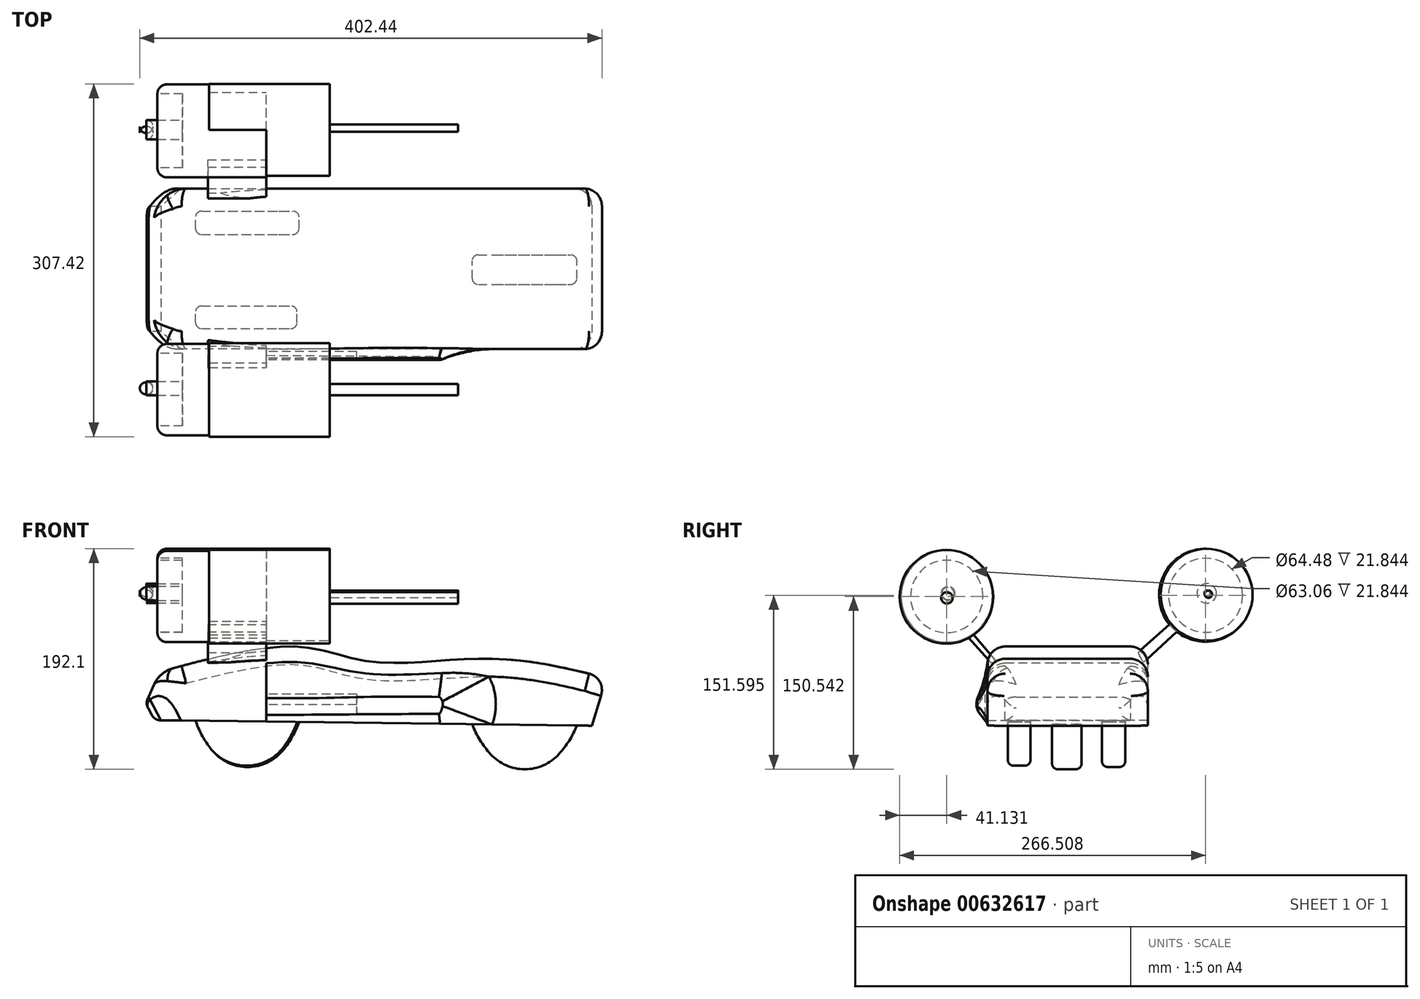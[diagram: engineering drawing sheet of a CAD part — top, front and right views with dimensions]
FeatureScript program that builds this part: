
annotation { "Feature Type Name" : "Feature", "Feature Type Description" : "" }
export const myFeature = defineFeature(function(context is Context, id is Id, definition is map)
    precondition{}
    {
        {
            var Q0;
            Q0=qCreatedBy(makeId("Front.planeOp"),FACE);
            var sketch = newSketch(context, id + "F0", { "sketchPlane" : qUnion([Q0])});
            skFitSpline(sketch, "E0", {"points": [v(-111.39, 0) * mm, v(28.2, 27.12) * mm, v(91.16, 14) * mm, v(196.58, 16.62) * mm, v(296.07, 0) * mm], "startDerivative": vector(527.44, 148.04) * mm, "endDerivative": vector(384.86, -95.59) * mm});
            skLineSegment(sketch, "E1", {"start": v(296.07, 0) * mm, "end": v(283.35, -41.68) * mm});
            skLineSegment(sketch, "E2", {"start": v(283.35, -41.68) * mm, "end": v(-91.68, -36.95) * mm});
            skLineSegment(sketch, "E3", {"start": v(-91.68, -36.95) * mm, "end": v(-111.39, 0) * mm});
            skSolve(sketch);
        }
        {
            var Q0;
            Q0 = qSketchRegion(id + "F0", true);
            extrude(context, id + "F1", {"entities" : qUnion([Q0]), "endBound" : BoundingType.SYMMETRIC, "oppositeDirection" : true, "depth" : 139.65 * mm, "offsetDistance" : 25.4 * mm});
        }
        {
            var Q0;
            Q0=makeQuery(id+"F1.opExtrude","CAP_EDGE",EDGE,{"disambiguationData":[OSD([sQuery(id+"F0.wireOp",EDGE,"E0")])],"isStart":false});
            var Q1;
            Q1=makeQuery(id+"F1.opExtrude","CAP_EDGE",EDGE,{"disambiguationData":[OSD([sQuery(id+"F0.wireOp",EDGE,"E0")])],"isStart":true});
            fillet(context, id + "F2", {"entities" : qUnion([Q0, Q1]), "radius" : 15.58 * mm, "tangentPropagation" : true, "allowEdgeOverflow" : false});
        }
        {
            var Q0;
            Q0=makeQuery(id+"F1.opExtrude","SWEPT_EDGE",EDGE,{"disambiguationData":[OSD([sQuery(id+"F0.wireOp",EDGE,"E0"),sQuery(id+"F0.wireOp",EDGE,"E1")])]});
            fillet(context, id + "F3", {"entities" : qUnion([Q0]), "radius" : 14.6 * mm, "tangentPropagation" : true, "allowEdgeOverflow" : false});
        }
        {
            var Q0;
            Q0=qCreatedBy(makeId("Right.planeOp"),FACE);
            var sketch = newSketch(context, id + "F4", { "sketchPlane" : qUnion([Q0])});
            skArc(sketch, "E4", {"start": v(-65.26, -9.54) * mm, "mid": v(-79.36, -22.04) * mm, "end": v(-66.86, -36.14) * mm});
            skLineSegment(sketch, "E5", {"start": v(-65.26, -9.54) * mm, "end": v(-66.06, -22.84) * mm});
            skLineSegment(sketch, "E6", {"start": v(-66.86, -36.14) * mm, "end": v(-66.06, -22.84) * mm});
            skSolve(sketch);
        }
        {
            var Q0;
            Q0 = qSketchRegion(id + "F4", true);
            extrude(context, id + "F5", {"entities" : qUnion([Q0]), "operationType" : NewBodyOperationType.ADD, "depth" : 159.32 * mm, "offsetDistance" : 25.4 * mm});
        }
        {
            var Q0;
            Q0=makeQuery(id+"F5.opExtrude","CAP_EDGE",EDGE,{"disambiguationData":[OSD([sQuery(id+"F4.wireOp",EDGE,"E4")])],"isStart":false});
            var Q1;
            Q1=makeQuery(id+"F3lUEw8ZCyhcsNu_1.1.F5.opExtrude","CAP_EDGE",EDGE,{"disambiguationData":[OSD([sQuery(id+"F4.wireOp",EDGE,"E4")])],"isStart":false});
            fillet(context, id + "F6", {"entities" : qUnion([Q0, Q1]), "radius" : 8.98 * mm, "tangentPropagation" : true, "allowEdgeOverflow" : false});
        }
        {
            var Q0;
            Q0=qCreatedBy(makeId("Right.planeOp"),FACE);
            var sketch = newSketch(context, id + "F7", { "sketchPlane" : qUnion([Q0])});
            skLineSegment(sketch, "E7", {"start": v(72.11, -14.5) * mm, "end": v(72.11, -32.7) * mm});
            skLineSegment(sketch, "E8", {"start": v(72.11, -32.7) * mm, "end": v(72.11, -23.6) * mm});
            skLineSegment(sketch, "E9", {"start": v(72.11, -23.6) * mm, "end": v(72.11, -32.7) * mm});
            skLineSegment(sketch, "E10", {"start": v(77.87, -23.6) * mm, "end": v(72.11, -32.7) * mm});
            skLineSegment(sketch, "E11", {"start": v(77.87, -23.6) * mm, "end": v(72.11, -14.5) * mm});
            skLineSegment(sketch, "E12", {"start": v(-72.12, -14.15) * mm, "end": v(-72.12, -32.4) * mm});
            skLineSegment(sketch, "E13", {"start": v(-72.12, -32.4) * mm, "end": v(-77.78, -23.27) * mm});
            skPoint(sketch, "E13.endSnap0", {"position": v(-72.12, -23.27) * mm});
            skLineSegment(sketch, "E14", {"start": v(-77.78, -23.27) * mm, "end": v(-72.12, -14.15) * mm});
            skSolve(sketch);
        }
        {
            var Q0;
            Q0 = qSketchRegion(id + "F7", true);
            extrude(context, id + "F8", {"entities" : qUnion([Q0]), "operationType" : NewBodyOperationType.REMOVE, "depth" : 78.65 * mm, "offsetDistance" : 25.4 * mm});
        }
        {
            var Q0;
            Q0=makeQuery(id+"F1.opExtrude","CAP_EDGE",EDGE,{"disambiguationData":[OSD([sQuery(id+"F0.wireOp",EDGE,"E3")])],"isStart":false});
            chamfer(context, id + "F9", {"entities" : qUnion([Q0]), "width" : 15.24 * mm, "tangentPropagation" : true});
        }
        {
            var Q0;
            {var subQ0=sQuery(id+"F0.wireOp",EDGE,"E0");Q0=makeQuery(id+"F9.opChamfer","BLEND_EDGE",EDGE,{"blendedFrom":[makeQuery(id+"F1.opExtrude","SWEPT_EDGE",EDGE,{"disambiguationData":[OSD([subQ0,sQuery(id+"F0.wireOp",EDGE,"E3")])]}),makeQuery(id+"F1.opExtrude","SWEPT_FACE",FACE,{"disambiguationData":[OSD([subQ0])]})],"blendedInto":[makeQuery(id+"F1.opExtrude","SWEPT_FACE",FACE,{"disambiguationData":[OSD([subQ0])]})]});}
            fillet(context, id + "F10", {"entities" : qUnion([Q0]), "radius" : 25.21 * mm, "tangentPropagation" : true, "allowEdgeOverflow" : false});
        }
        {
            var Q0;
            Q0=qCreatedBy(makeId("Front.planeOp"),FACE);
            var sketch = newSketch(context, id + "F11", { "sketchPlane" : qUnion([Q0])});
            skLineSegment(sketch, "E15", {"start": v(19.53, 27.35) * mm, "end": v(103, 49.29) * mm});
            skLineSegment(sketch, "E16", {"start": v(103, 49.29) * mm, "end": v(187, 37.43) * mm});
            skLineSegment(sketch, "E17", {"start": v(187, 37.43) * mm, "end": v(228.55, 13.52) * mm});
            skLineSegment(sketch, "E18", {"start": v(228.55, 13.52) * mm, "end": v(82.33, 13.52) * mm});
            skLineSegment(sketch, "E19", {"start": v(82.33, 13.52) * mm, "end": v(19.53, 27.35) * mm});
            skSolve(sketch);
        }
        {
            var Q0;
            Q0=makeQuery(id+"F5.boolean.opBoolean","INTERSECT",EDGE,{"disambiguationData":[OD(1.0)],"derivedFrom":[makeQuery(id+"F1.opExtrude","CAP_FACE",FACE,{"disambiguationData":[OSD([sQuery(id+"F0.wireOp",EDGE,"E0"),sQuery(id+"F0.wireOp",EDGE,"E1"),sQuery(id+"F0.wireOp",EDGE,"E2"),sQuery(id+"F0.wireOp",EDGE,"E3")])],"isStart":true}),makeQuery(id+"F5.opExtrude","SWEPT_FACE",FACE,{"disambiguationData":[OSD([sQuery(id+"F4.wireOp",EDGE,"E4")])]})]});
            var Q1;
            Q1=makeQuery(id+"F3lUEw8ZCyhcsNu_1.1.F5.boolean.opBoolean","INTERSECT",EDGE,{"disambiguationData":[OD(1.0)],"derivedFrom":[makeQuery(id+"F1.opExtrude","CAP_FACE",FACE,{"disambiguationData":[OSD([sQuery(id+"F0.wireOp",EDGE,"E0"),sQuery(id+"F0.wireOp",EDGE,"E1"),sQuery(id+"F0.wireOp",EDGE,"E2"),sQuery(id+"F0.wireOp",EDGE,"E3")])],"isStart":false}),makeQuery(id+"F3lUEw8ZCyhcsNu_1.1.F5.opExtrude","SWEPT_FACE",FACE,{"disambiguationData":[OSD([sQuery(id+"F4.wireOp",EDGE,"E4")])]})]});
            fillet(context, id + "F12", {"entities" : qUnion([Q0, Q1]), "radius" : 123.76 * mm, "tangentPropagation" : true, "allowEdgeOverflow" : false});
        }
        {
            var Q0;
            Q0=qCreatedBy(makeId("Top.planeOp"),FACE);
            var sketch = newSketch(context, id + "F13", { "sketchPlane" : qUnion([Q0])});
            skLineSegment(sketch, "E20.bottom", {"start": v(-61.68, -52) * mm, "end": v(26.68, -52) * mm});
            skLineSegment(sketch, "E20.top", {"start": v(-61.68, -32.34) * mm, "end": v(26.68, -32.34) * mm});
            skLineSegment(sketch, "E20.left", {"start": v(-61.68, -52) * mm, "end": v(-61.68, -32.34) * mm});
            skLineSegment(sketch, "E20.right", {"start": v(26.68, -52) * mm, "end": v(26.68, -32.34) * mm});
            skLineSegment(sketch, "E21.bottom", {"start": v(-61.68, 29.92) * mm, "end": v(28.42, 29.92) * mm});
            skLineSegment(sketch, "E21.top", {"start": v(-61.68, 50.23) * mm, "end": v(28.42, 50.23) * mm});
            skLineSegment(sketch, "E21.left", {"start": v(-61.68, 29.92) * mm, "end": v(-61.68, 50.23) * mm});
            skLineSegment(sketch, "E21.right", {"start": v(28.42, 29.92) * mm, "end": v(28.42, 50.23) * mm});
            skLineSegment(sketch, "E22.bottom", {"start": v(179.16, -13.58) * mm, "end": v(270.37, -13.58) * mm});
            skLineSegment(sketch, "E22.top", {"start": v(179.16, 12.15) * mm, "end": v(270.37, 12.15) * mm});
            skLineSegment(sketch, "E22.left", {"start": v(179.16, -13.58) * mm, "end": v(179.16, 12.15) * mm});
            skLineSegment(sketch, "E22.right", {"start": v(270.37, -13.58) * mm, "end": v(270.37, 12.15) * mm});
            skSolve(sketch);
        }
        {
            var Q0;
            Q0 = qSketchRegion(id + "F13", true);
            extrude(context, id + "F14", {"entities" : qUnion([Q0]), "operationType" : NewBodyOperationType.ADD, "oppositeDirection" : true, "depth" : 93.8 * mm, "offsetDistance" : 25.4 * mm});
        }
        {
            var Q0;
            Q0=makeQuery(id+"F14.opExtrude","CAP_EDGE",EDGE,{"disambiguationData":[OSD([sQuery(id+"F13.wireOp",EDGE,"E21.left")])],"isStart":false});
            var Q1;
            Q1=makeQuery(id+"F14.opExtrude","CAP_EDGE",EDGE,{"disambiguationData":[OSD([sQuery(id+"F13.wireOp",EDGE,"E20.left")])],"isStart":false});
            var Q2;
            Q2=makeQuery(id+"F14.opExtrude","CAP_EDGE",EDGE,{"disambiguationData":[OSD([sQuery(id+"F13.wireOp",EDGE,"E21.right")])],"isStart":false});
            var Q3;
            Q3=makeQuery(id+"F14.opExtrude","CAP_EDGE",EDGE,{"disambiguationData":[OSD([sQuery(id+"F13.wireOp",EDGE,"E20.right")])],"isStart":false});
            var Q4;
            Q4=makeQuery(id+"F14.opExtrude","CAP_EDGE",EDGE,{"disambiguationData":[OSD([sQuery(id+"F13.wireOp",EDGE,"E22.left")])],"isStart":false});
            var Q5;
            Q5=makeQuery(id+"F14.opExtrude","CAP_EDGE",EDGE,{"disambiguationData":[OSD([sQuery(id+"F13.wireOp",EDGE,"E22.right")])],"isStart":false});
            fillet(context, id + "F15", {"entities" : qUnion([Q0, Q1, Q2, Q3, Q4, Q5]), "radius" : 83.48 * mm, "tangentPropagation" : true, "allowEdgeOverflow" : false});
        }
        {
            var Q0;
            Q0=makeQuery(id+"F15.opFillet","BLEND_EDGE",EDGE,{"blendedFrom":[makeQuery(id+"F14.opExtrude","CAP_EDGE",EDGE,{"disambiguationData":[OSD([sQuery(id+"F13.wireOp",EDGE,"E22.left")])],"isStart":false}),makeQuery(id+"F14.opExtrude","CAP_EDGE",EDGE,{"disambiguationData":[OSD([sQuery(id+"F13.wireOp",EDGE,"E22.right")])],"isStart":false})],"blendedInto":[]});
            var Q1;
            Q1=makeQuery(id+"F15.opFillet","BLEND_EDGE",EDGE,{"blendedFrom":[makeQuery(id+"F14.opExtrude","CAP_EDGE",EDGE,{"disambiguationData":[OSD([sQuery(id+"F13.wireOp",EDGE,"E21.left")])],"isStart":false}),makeQuery(id+"F14.opExtrude","CAP_EDGE",EDGE,{"disambiguationData":[OSD([sQuery(id+"F13.wireOp",EDGE,"E21.right")])],"isStart":false})],"blendedInto":[]});
            var Q2;
            Q2=makeQuery(id+"F15.opFillet","BLEND_EDGE",EDGE,{"blendedFrom":[makeQuery(id+"F14.opExtrude","CAP_EDGE",EDGE,{"disambiguationData":[OSD([sQuery(id+"F13.wireOp",EDGE,"E20.left")])],"isStart":false}),makeQuery(id+"F14.opExtrude","CAP_EDGE",EDGE,{"disambiguationData":[OSD([sQuery(id+"F13.wireOp",EDGE,"E20.right")])],"isStart":false})],"blendedInto":[]});
            fillet(context, id + "F16", {"entities" : qUnion([Q0, Q1, Q2]), "radius" : 40.13 * mm, "tangentPropagation" : true, "allowEdgeOverflow" : false});
        }
        {
            var Q0;
            Q0=makeQuery(id+"F15.opFillet","BLEND_EDGE",EDGE,{"blendedFrom":[makeQuery(id+"F14.opExtrude","CAP_EDGE",EDGE,{"disambiguationData":[OSD([sQuery(id+"F13.wireOp",EDGE,"E21.right")])],"isStart":false}),makeQuery(id+"F14.opExtrude","SWEPT_FACE",FACE,{"disambiguationData":[OSD([sQuery(id+"F13.wireOp",EDGE,"E21.top")])]})],"blendedInto":[makeQuery(id+"F14.opExtrude","SWEPT_FACE",FACE,{"disambiguationData":[OSD([sQuery(id+"F13.wireOp",EDGE,"E21.top")])]})]});
            var Q1;
            Q1=makeQuery(id+"F15.opFillet","BLEND_EDGE",EDGE,{"blendedFrom":[makeQuery(id+"F14.opExtrude","CAP_EDGE",EDGE,{"disambiguationData":[OSD([sQuery(id+"F13.wireOp",EDGE,"E20.right")])],"isStart":false}),makeQuery(id+"F14.opExtrude","SWEPT_FACE",FACE,{"disambiguationData":[OSD([sQuery(id+"F13.wireOp",EDGE,"E20.top")])]})],"blendedInto":[makeQuery(id+"F14.opExtrude","SWEPT_FACE",FACE,{"disambiguationData":[OSD([sQuery(id+"F13.wireOp",EDGE,"E20.top")])]})]});
            var Q2;
            Q2=makeQuery(id+"F15.opFillet","BLEND_EDGE",EDGE,{"blendedFrom":[makeQuery(id+"F14.opExtrude","CAP_EDGE",EDGE,{"disambiguationData":[OSD([sQuery(id+"F13.wireOp",EDGE,"E22.right")])],"isStart":false}),makeQuery(id+"F14.opExtrude","SWEPT_FACE",FACE,{"disambiguationData":[OSD([sQuery(id+"F13.wireOp",EDGE,"E22.top")])]})],"blendedInto":[makeQuery(id+"F14.opExtrude","SWEPT_FACE",FACE,{"disambiguationData":[OSD([sQuery(id+"F13.wireOp",EDGE,"E22.top")])]})]});
            var Q3;
            Q3=makeQuery(id+"F15.opFillet","BLEND_EDGE",EDGE,{"blendedFrom":[makeQuery(id+"F14.opExtrude","CAP_EDGE",EDGE,{"disambiguationData":[OSD([sQuery(id+"F13.wireOp",EDGE,"E22.right")])],"isStart":false}),makeQuery(id+"F14.opExtrude","SWEPT_FACE",FACE,{"disambiguationData":[OSD([sQuery(id+"F13.wireOp",EDGE,"E22.bottom")])]})],"blendedInto":[makeQuery(id+"F14.opExtrude","SWEPT_FACE",FACE,{"disambiguationData":[OSD([sQuery(id+"F13.wireOp",EDGE,"E22.bottom")])]})]});
            var Q4;
            Q4=makeQuery(id+"F15.opFillet","BLEND_EDGE",EDGE,{"blendedFrom":[makeQuery(id+"F14.opExtrude","CAP_EDGE",EDGE,{"disambiguationData":[OSD([sQuery(id+"F13.wireOp",EDGE,"E20.right")])],"isStart":false}),makeQuery(id+"F14.opExtrude","SWEPT_FACE",FACE,{"disambiguationData":[OSD([sQuery(id+"F13.wireOp",EDGE,"E20.bottom")])]})],"blendedInto":[makeQuery(id+"F14.opExtrude","SWEPT_FACE",FACE,{"disambiguationData":[OSD([sQuery(id+"F13.wireOp",EDGE,"E20.bottom")])]})]});
            var Q5;
            Q5=makeQuery(id+"F15.opFillet","BLEND_EDGE",EDGE,{"blendedFrom":[makeQuery(id+"F14.opExtrude","CAP_EDGE",EDGE,{"disambiguationData":[OSD([sQuery(id+"F13.wireOp",EDGE,"E21.right")])],"isStart":false}),makeQuery(id+"F14.opExtrude","SWEPT_FACE",FACE,{"disambiguationData":[OSD([sQuery(id+"F13.wireOp",EDGE,"E21.bottom")])]})],"blendedInto":[makeQuery(id+"F14.opExtrude","SWEPT_FACE",FACE,{"disambiguationData":[OSD([sQuery(id+"F13.wireOp",EDGE,"E21.bottom")])]})]});
            fillet(context, id + "F17", {"entities" : qUnion([Q0, Q1, Q2, Q3, Q4, Q5]), "radius" : 5.08 * mm, "tangentPropagation" : true, "allowEdgeOverflow" : false});
        }
        {
            var Q0;
            Q0=sQuery(id+"F11.wireOp",EDGE,"E15");
            var Q1;
            Q1=sQuery(id+"F11.wireOp",EDGE,"E19");
            var Q2;
            Q2=sQuery(id+"F11.wireOp",EDGE,"E18");
            var Q3;
            Q3=sQuery(id+"F11.wireOp",EDGE,"E17");
            var Q4;
            Q4=sQuery(id+"F11.wireOp",EDGE,"E16");
            extrude(context, id + "F18", {"bodyType" : ToolBodyType.SURFACE, "surfaceEntities" : qUnion([Q0, Q1, Q2, Q3, Q4]), "endBound" : BoundingType.SYMMETRIC, "depth" : 100.02 * mm, "offsetDistance" : 25.4 * mm});
        }
        {
            var Q0;
            Q0=qCreatedBy(makeId("Right.planeOp"),FACE);
            var sketch = newSketch(context, id + "F19", { "sketchPlane" : qUnion([Q0])});
            skLineSegment(sketch, "E23", {"start": v(65.95, 13.38) * mm, "end": v(109.33, 53.33) * mm});
            skLineSegment(sketch, "E24", {"start": v(109.33, 53.33) * mm, "end": v(103.43, 59.64) * mm});
            skLineSegment(sketch, "E25", {"start": v(103.43, 59.64) * mm, "end": v(61.2, 21.9) * mm});
            skLineSegment(sketch, "E26", {"start": v(61.2, 21.9) * mm, "end": v(65.95, 13.38) * mm});
            skLineSegment(sketch, "E27", {"start": v(-60.68, 12.45) * mm, "end": v(-67.27, 13.56) * mm});
            skLineSegment(sketch, "E28", {"start": v(-67.27, 13.56) * mm, "end": v(-103.78, 54.83) * mm});
            skLineSegment(sketch, "E29", {"start": v(-103.78, 54.83) * mm, "end": v(-105.55, 65.9) * mm});
            skLineSegment(sketch, "E30", {"start": v(-105.55, 65.9) * mm, "end": v(-60.68, 12.45) * mm});
            skCircle(sketch, "E31", {"center": v(121.04, 72.42) * mm, "radius": 40.04 * mm});
            skCircle(sketch, "E32", {"center": v(-105.55, 70.64) * mm, "radius": 40.8 * mm});
            skSolve(sketch);
        }
        {
            var Q0;
            {var subQ0=sQuery(id+"F19.wireOp",EDGE,"E24");Q0=makeQuery(id+"F19.imprint","IMPRINT",FACE,{"disambiguationData":[TD([[makeQuery(id+"F19.imprint","IMPRINT",EDGE,{"derivedFrom":subQ0}),1.0]])]});}
            var Q1;
            {var subQ0=sQuery(id+"F19.wireOp",EDGE,"E26");Q1=makeQuery(id+"F19.imprint","IMPRINT",FACE,{"disambiguationData":[TD([[makeQuery(id+"F19.imprint","IMPRINT",EDGE,{"derivedFrom":subQ0}),1.0]])]});}
            var Q2;
            {var subQ0=sQuery(id+"F19.wireOp",EDGE,"E27");Q2=makeQuery(id+"F19.imprint","IMPRINT",FACE,{"disambiguationData":[TD([[makeQuery(id+"F19.imprint","IMPRINT",EDGE,{"derivedFrom":subQ0}),-1.0]])]});}
            var Q3;
            {var subQ0=sQuery(id+"F19.wireOp",EDGE,"E29");Q3=makeQuery(id+"F19.imprint","IMPRINT",FACE,{"disambiguationData":[TD([[makeQuery(id+"F19.imprint","IMPRINT",EDGE,{"derivedFrom":subQ0}),-1.0]])]});}
            extrude(context, id + "F20", {"entities" : qUnion([Q0, Q1, Q2, Q3]), "operationType" : NewBodyOperationType.ADD, "oppositeDirection" : true, "depth" : 50.96 * mm, "offsetDistance" : 25.4 * mm});
        }
        {
            var Q0;
            {var subQ0=sQuery(id+"F19.wireOp",EDGE,"E24");Q0=makeQuery(id+"F19.imprint","IMPRINT",FACE,{"disambiguationData":[TD([[makeQuery(id+"F19.imprint","IMPRINT",EDGE,{"derivedFrom":subQ0}),-1.0]])]});}
            var Q1;
            {var subQ0=sQuery(id+"F19.wireOp",EDGE,"E29");Q1=makeQuery(id+"F19.imprint","IMPRINT",FACE,{"disambiguationData":[TD([[makeQuery(id+"F19.imprint","IMPRINT",EDGE,{"derivedFrom":subQ0}),1.0]])]});}
            extrude(context, id + "F21", {"entities" : qUnion([Q0, Q1]), "operationType" : NewBodyOperationType.ADD, "oppositeDirection" : true, "depth" : 49.86 * mm, "offsetDistance" : 25.4 * mm});
        }
        {
            var Q0;
            {var subQ0=sQuery(id+"F19.wireOp",EDGE,"E24");Q0=makeQuery(id+"F19.imprint","IMPRINT",FACE,{"disambiguationData":[TD([[makeQuery(id+"F19.imprint","IMPRINT",EDGE,{"derivedFrom":subQ0}),-1.0]])]});}
            var Q1;
            {var subQ0=sQuery(id+"F19.wireOp",EDGE,"E29");Q1=makeQuery(id+"F19.imprint","IMPRINT",FACE,{"disambiguationData":[TD([[makeQuery(id+"F19.imprint","IMPRINT",EDGE,{"derivedFrom":subQ0}),1.0]])]});}
            var Q2;
            {var subQ0=sQuery(id+"F19.wireOp",EDGE,"E29");Q2=makeQuery(id+"F19.imprint","IMPRINT",FACE,{"disambiguationData":[TD([[makeQuery(id+"F19.imprint","IMPRINT",EDGE,{"derivedFrom":subQ0}),-1.0]])]});}
            var Q3;
            {var subQ0=sQuery(id+"F19.wireOp",EDGE,"E24");Q3=makeQuery(id+"F19.imprint","IMPRINT",FACE,{"disambiguationData":[TD([[makeQuery(id+"F19.imprint","IMPRINT",EDGE,{"derivedFrom":subQ0}),1.0]])]});}
            extrude(context, id + "F22", {"entities" : qUnion([Q0, Q1, Q2, Q3]), "operationType" : NewBodyOperationType.ADD, "depth" : 55.22 * mm, "offsetDistance" : 25.4 * mm});
        }
        {
            var Q0;
            Q0=qCreatedBy(makeId("Right.planeOp"),FACE);
            var sketch = newSketch(context, id + "F23", { "sketchPlane" : qUnion([Q0])});
            skCircle(sketch, "E33", {"center": v(-105.02, 70.59) * mm, "radius": 28.06 * mm});
            skCircle(sketch, "E34", {"center": v(-105.02, 70.59) * mm, "radius": 13.97 * mm});
            skCircle(sketch, "E35", {"center": v(121.55, 72.17) * mm, "radius": 26.48 * mm});
            skCircle(sketch, "E36", {"center": v(121.55, 72.17) * mm, "radius": 13.98 * mm});
            skSolve(sketch);
        }
        {
            var Q0;
            Q0=sQuery(id+"F23.wireOp",EDGE,"E33");
            var Q1;
            Q1=sQuery(id+"F23.wireOp",EDGE,"E35");
            extrude(context, id + "F24", {"bodyType" : ToolBodyType.SURFACE, "surfaceEntities" : qUnion([Q0, Q1]), "depth" : 97.47 * mm, "offsetDistance" : 25.4 * mm});
        }
        {
            var Q0;
            Q0=sQuery(id+"F23.wireOp",EDGE,"E36");
            var Q1;
            Q1=sQuery(id+"F23.wireOp",EDGE,"E34");
            extrude(context, id + "F25", {"bodyType" : ToolBodyType.SURFACE, "surfaceEntities" : qUnion([Q0, Q1]), "depth" : 146.7 * mm, "offsetDistance" : 25.4 * mm});
        }
        {
            var Q0;
            Q0=qCreatedBy(makeId("Right.planeOp"),FACE);
            var sketch = newSketch(context, id + "F26", { "sketchPlane" : qUnion([Q0])});
            skCircle(sketch, "E37", {"center": v(120.17, 71.97) * mm, "radius": 40.5 * mm});
            skCircle(sketch, "E38", {"center": v(-105.2, 70.91) * mm, "radius": 39.8 * mm});
            skSolve(sketch);
        }
        {
            var Q0;
            Q0 = qSketchRegion(id + "F26", true);
            extrude(context, id + "F27", {"entities" : qUnion([Q0]), "operationType" : NewBodyOperationType.ADD, "oppositeDirection" : true, "depth" : 94.92 * mm, "offsetDistance" : 25.4 * mm});
        }
        {
            var Q0;
            Q0=makeQuery(id+"F27.opExtrude","CAP_EDGE",EDGE,{"disambiguationData":[OSD([sQuery(id+"F26.wireOp",EDGE,"E37")])],"isStart":false});
            var Q1;
            Q1=makeQuery(id+"F27.opExtrude","CAP_EDGE",EDGE,{"disambiguationData":[OSD([sQuery(id+"F26.wireOp",EDGE,"E38")])],"isStart":false});
            fillet(context, id + "F28", {"entities" : qUnion([Q0, Q1]), "radius" : 8.26 * mm, "tangentPropagation" : true, "allowEdgeOverflow" : false});
        }
        {
            var Q0;
            Q0=makeQuery(id+"F27.opExtrude","CAP_FACE",FACE,{"disambiguationData":[OSD([sQuery(id+"F26.wireOp",EDGE,"E37")])],"isStart":false});
            var Q1;
            Q1=makeQuery(id+"F27.opExtrude","CAP_FACE",FACE,{"disambiguationData":[OSD([sQuery(id+"F26.wireOp",EDGE,"E38")])],"isStart":false});
            extrude(context, id + "F29", {"entities" : qUnion([Q0, Q1]), "operationType" : NewBodyOperationType.REMOVE, "oppositeDirection" : true, "depth" : 21.84 * mm, "offsetDistance" : 25.4 * mm});
        }
        {
            var Q0;
            Q0=qCreatedBy(makeId("Right.planeOp"),FACE);
            var sketch = newSketch(context, id + "F30", { "sketchPlane" : qUnion([Q0])});
            skCircle(sketch, "E39", {"center": v(121.18, 73.6) * mm, "radius": 8.49 * mm});
            skCircle(sketch, "E40", {"center": v(-104.1, 73.62) * mm, "radius": 6.08 * mm});
            skSolve(sketch);
        }
        {
            var Q0;
            Q0 = qSketchRegion(id + "F30", true);
            extrude(context, id + "F31", {"entities" : qUnion([Q0]), "operationType" : NewBodyOperationType.ADD, "oppositeDirection" : true, "depth" : 110.23 * mm, "offsetDistance" : 25.4 * mm});
        }
        {
            var Q0;
            Q0=makeQuery(id+"F31.opExtrude","CAP_EDGE",EDGE,{"disambiguationData":[OSD([sQuery(id+"F30.wireOp",EDGE,"E40")])],"isStart":false});
            var Q1;
            Q1=makeQuery(id+"F31.opExtrude","CAP_EDGE",EDGE,{"disambiguationData":[OSD([sQuery(id+"F30.wireOp",EDGE,"E39")])],"isStart":false});
            fillet(context, id + "F32", {"entities" : qUnion([Q0, Q1]), "radius" : 5.7 * mm, "tangentPropagation" : true, "allowEdgeOverflow" : false});
        }
        {
            var Q0;
            Q0=qCreatedBy(makeId("Right.planeOp"),FACE);
            var sketch = newSketch(context, id + "F33", { "sketchPlane" : qUnion([Q0])});
            skCircle(sketch, "E41", {"center": v(-105.13, 69.68) * mm, "radius": 4.97 * mm});
            skCircle(sketch, "E42", {"center": v(122.6, 72.92) * mm, "radius": 3.19 * mm});
            skSolve(sketch);
        }
        {
            var Q0;
            Q0 = qSketchRegion(id + "F33", true);
            extrude(context, id + "F34", {"entities" : qUnion([Q0]), "operationType" : NewBodyOperationType.ADD, "depth" : 166.9 * mm, "offsetDistance" : 25.4 * mm});
        }
        {
            var Q0;
            Q0=makeQuery(id+"F1.opExtrude","SWEPT_FACE",FACE,{"disambiguationData":[OSD([sQuery(id+"F0.wireOp",EDGE,"E3")])]});
            extrude(context, id + "F35", {"entities" : qUnion([Q0]), "operationType" : NewBodyOperationType.ADD, "depth" : 5 * mm, "offsetDistance" : 25.4 * mm});
        }
        {
            var Q0;
            {var subQ0=sQuery(id+"F0.wireOp",EDGE,"E3");var subQ1=sQuery(id+"F0.wireOp",EDGE,"E0");Q0=makeQuery(id+"F35.opExtrude","CAP_EDGE",EDGE,{"disambiguationData":[OSD([subQ1,subQ0]),TDD([makeQuery(id+"F9.opChamfer","BLEND_EDGE",EDGE,{"blendedFrom":[makeQuery(id+"F1.opExtrude","SWEPT_EDGE",EDGE,{"disambiguationData":[OSD([subQ1,subQ0])]}),makeQuery(id+"F1.opExtrude","SWEPT_FACE",FACE,{"disambiguationData":[OSD([subQ0])]})],"blendedInto":[makeQuery(id+"F1.opExtrude","SWEPT_FACE",FACE,{"disambiguationData":[OSD([subQ0])]})]})])],"isStart":false});}
            var Q1;
            {var subQ0=sQuery(id+"F0.wireOp",EDGE,"E3");Q1=makeQuery(id+"F35.opExtrude","CAP_EDGE",EDGE,{"disambiguationData":[OSD([subQ0]),TDD([makeQuery(id+"F9.opChamfer","BLEND_EDGE",EDGE,{"blendedFrom":[makeQuery(id+"F1.opExtrude","CAP_EDGE",EDGE,{"disambiguationData":[OSD([subQ0])],"isStart":false}),makeQuery(id+"F1.opExtrude","SWEPT_FACE",FACE,{"disambiguationData":[OSD([subQ0])]})],"blendedInto":[makeQuery(id+"F1.opExtrude","SWEPT_FACE",FACE,{"disambiguationData":[OSD([subQ0])]})]})])],"isStart":false});}
            var Q2;
            Q2=makeQuery(id+"F35.opExtrude","CAP_EDGE",EDGE,{"disambiguationData":[OSD([sQuery(id+"F0.wireOp",EDGE,"E2"),sQuery(id+"F0.wireOp",EDGE,"E3")])],"isStart":false});
            var Q3;
            {var subQ0=sQuery(id+"F0.wireOp",EDGE,"E3");Q3=makeQuery(id+"F35.opExtrude","CAP_EDGE",EDGE,{"disambiguationData":[OSD([subQ0]),TDD([makeQuery(id+"F9.opChamfer","BLEND_EDGE",EDGE,{"blendedFrom":[makeQuery(id+"F1.opExtrude","CAP_EDGE",EDGE,{"disambiguationData":[OSD([subQ0])],"isStart":true}),makeQuery(id+"F1.opExtrude","SWEPT_FACE",FACE,{"disambiguationData":[OSD([subQ0])]})],"blendedInto":[makeQuery(id+"F1.opExtrude","SWEPT_FACE",FACE,{"disambiguationData":[OSD([subQ0])]})]})])],"isStart":false});}
            fillet(context, id + "F36", {"entities" : qUnion([Q0, Q1, Q2, Q3]), "radius" : 8.58 * mm, "tangentPropagation" : true, "allowEdgeOverflow" : false});
        }
    });
